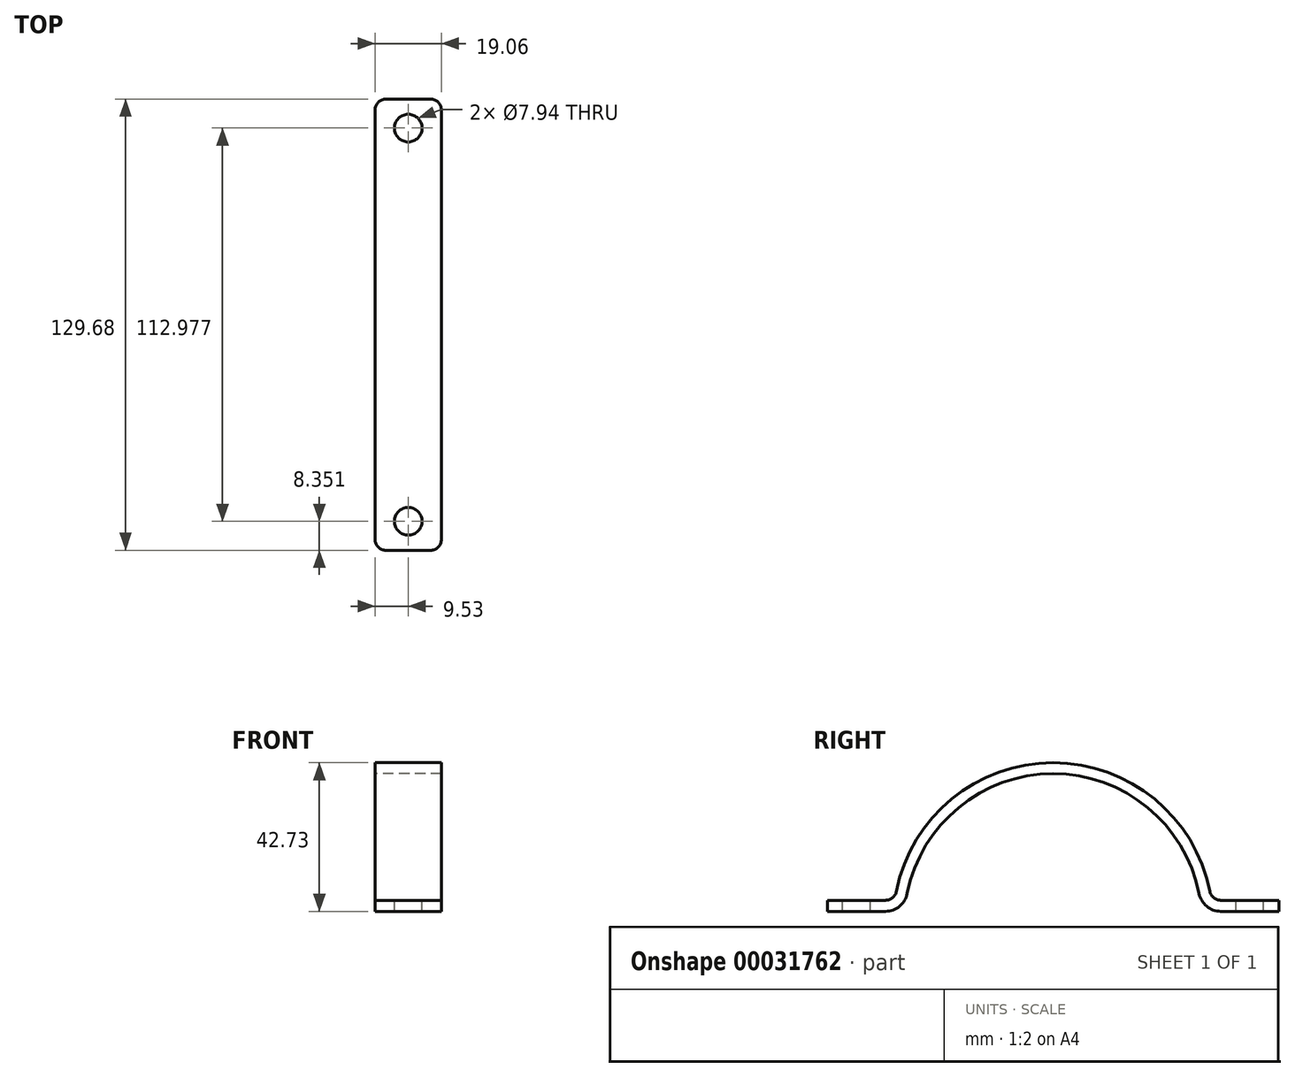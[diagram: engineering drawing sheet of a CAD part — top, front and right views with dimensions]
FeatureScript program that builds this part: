
annotation { "Feature Type Name" : "Feature", "Feature Type Description" : "" }
export const myFeature = defineFeature(function(context is Context, id is Id, definition is map)
    precondition{}
    {
        {
            var Q0;
            Q0=qCreatedBy(makeId("Right.planeOp"),FACE);
            var sketch = newSketch(context, id + "F0", { "sketchPlane" : qUnion([Q0])});
            skArc(sketch, "E0", {"start": v(42.6, 3.17) * mm, "mid": v(0, 42.72) * mm, "end": v(-42.6, 3.17) * mm});
            skArc(sketch, "E1", {"start": v(45.46, 6.35) * mm, "mid": v(0, 45.9) * mm, "end": v(-45.46, 6.35) * mm});
            skLineSegment(sketch, "E2.0", {"start": v(-64.84, 3.18) * mm, "end": v(-42.6, 3.18) * mm});
            skLineSegment(sketch, "E3.0", {"start": v(-64.84, 6.35) * mm, "end": v(-45.46, 6.35) * mm});
            skLineSegment(sketch, "E4", {"start": v(-45.79, 3.18) * mm, "end": v(-45.79, -9.23) * mm});
            skLineSegment(sketch, "E5.0", {"start": v(-64.84, 6.35) * mm, "end": v(-64.84, 3.18) * mm});
            skLineSegment(sketch, "E6", {"start": v(0, 0) * mm, "end": v(0, -29.1) * mm, "construction": true});
            skLineSegment(sketch, "E7.MirrorCS", {"start": v(64.84, 6.35) * mm, "end": v(64.84, 3.18) * mm});
            skLineSegment(sketch, "E8.trimOffspring", {"start": v(45.46, 6.35) * mm, "end": v(64.84, 6.35) * mm});
            skLineSegment(sketch, "E9.trimOffspring", {"start": v(42.6, 3.18) * mm, "end": v(64.84, 3.18) * mm});
            skSolve(sketch);
        }
        {
            var Q0;
            Q0=qSketchRegion(id+"F0",true);
            extrude(context, id + "F1", {"entities" : qUnion([Q0]), "endBound" : BoundingType.SYMMETRIC, "depth" : 19.05 * mm});
        }
        {
            var Q0;
            Q0=makeQuery(id+"F1.opExtrude","SWEPT_EDGE",EDGE,{"disambiguationData":[OSD([sQuery(id+"F0.wireOp",EDGE,"E1"),sQuery(id+"F0.wireOp",EDGE,"E8.trimOffspring")])]});
            var Q1;
            Q1=makeQuery(id+"F1.opExtrude","SWEPT_EDGE",EDGE,{"disambiguationData":[OSD([sQuery(id+"F0.wireOp",EDGE,"E1"),sQuery(id+"F0.wireOp",EDGE,"E3.0")])]});
            fillet(context, id + "F2", {"entities" : qUnion([Q0, Q1]), "radius" : 3.17 * mm, "tangentPropagation" : true, "allowEdgeOverflow" : false});
        }
        {
            var Q0;
            Q0=makeQuery(id+"F1.opExtrude","SWEPT_EDGE",EDGE,{"disambiguationData":[OSD([sQuery(id+"F0.wireOp",EDGE,"E0"),sQuery(id+"F0.wireOp",EDGE,"E2.0")])]});
            var Q1;
            Q1=makeQuery(id+"F1.opExtrude","SWEPT_EDGE",EDGE,{"disambiguationData":[OSD([sQuery(id+"F0.wireOp",EDGE,"E0"),sQuery(id+"F0.wireOp",EDGE,"E9.trimOffspring")])]});
            fillet(context, id + "F3", {"entities" : qUnion([Q0, Q1]), "radius" : 6.35 * mm, "tangentPropagation" : true, "allowEdgeOverflow" : false});
        }
        {
            var Q0;
            Q0=makeQuery(id+"F1.opExtrude","CAP_EDGE",EDGE,{"disambiguationData":[OSD([sQuery(id+"F0.wireOp",EDGE,"E7.MirrorCS")])],"isStart":false});
            var Q1;
            Q1=makeQuery(id+"F1.opExtrude","CAP_EDGE",EDGE,{"disambiguationData":[OSD([sQuery(id+"F0.wireOp",EDGE,"E7.MirrorCS")])],"isStart":true});
            var Q2;
            Q2=makeQuery(id+"F1.opExtrude","CAP_EDGE",EDGE,{"disambiguationData":[OSD([sQuery(id+"F0.wireOp",EDGE,"E5.0")])],"isStart":false});
            var Q3;
            Q3=makeQuery(id+"F1.opExtrude","CAP_EDGE",EDGE,{"disambiguationData":[OSD([sQuery(id+"F0.wireOp",EDGE,"E5.0")])],"isStart":true});
            fillet(context, id + "F4", {"entities" : qUnion([Q0, Q1, Q2, Q3]), "radius" : 3.17 * mm, "tangentPropagation" : true, "allowEdgeOverflow" : false});
        }
        {
            var Q0;
            Q0=makeQuery(id+"F1.opExtrude","SWEPT_FACE",FACE,{"disambiguationData":[OSD([sQuery(id+"F0.wireOp",EDGE,"E3.0")])]});
            var sketch = newSketch(context, id + "F5", { "sketchPlane" : qUnion([Q0])});
            skLineSegment(sketch, "E10", {"start": v(0, -48.14) * mm, "end": v(0, -64.84) * mm, "construction": true});
            skPoint(sketch, "E11", {"position": v(0, -56.49) * mm});
            skLineSegment(sketch, "E12", {"start": v(0, 0) * mm, "end": v(35.3, 0) * mm, "construction": true});
            skPoint(sketch, "E13.MirrorP", {"position": v(0, 56.49) * mm});
            skSolve(sketch);
        }
        {
            var Q0;
            Q0=sQuery(id+"F5.wireOp",VERTEX,"E11");
            var Q1;
            Q1=sQuery(id+"F5.wireOp",VERTEX,"E13.MirrorP");
            var Q2;
            Q2=makeQuery(id+"F1.opExtrude","SWEPT_BODY",BODY,{"disambiguationData":[OSD([sQuery(id+"F0.wireOp",EDGE,"E0"),sQuery(id+"F0.wireOp",EDGE,"E1"),sQuery(id+"F0.wireOp",EDGE,"E2.0"),sQuery(id+"F0.wireOp",EDGE,"E3.0"),sQuery(id+"F0.wireOp",EDGE,"E5.0"),sQuery(id+"F0.wireOp",EDGE,"E7.MirrorCS"),sQuery(id+"F0.wireOp",EDGE,"E8.trimOffspring"),sQuery(id+"F0.wireOp",EDGE,"E9.trimOffspring")])]});
            hole(context, id + "F6", {"style" : HoleStyle.SIMPLE, "holeDiameter" : 7.94 * mm, "endStyle" : HoleEndStyle.THROUGH, "locations" : qUnion([Q0, Q1]), "scope" : qUnion([Q2])});
        }
    });
